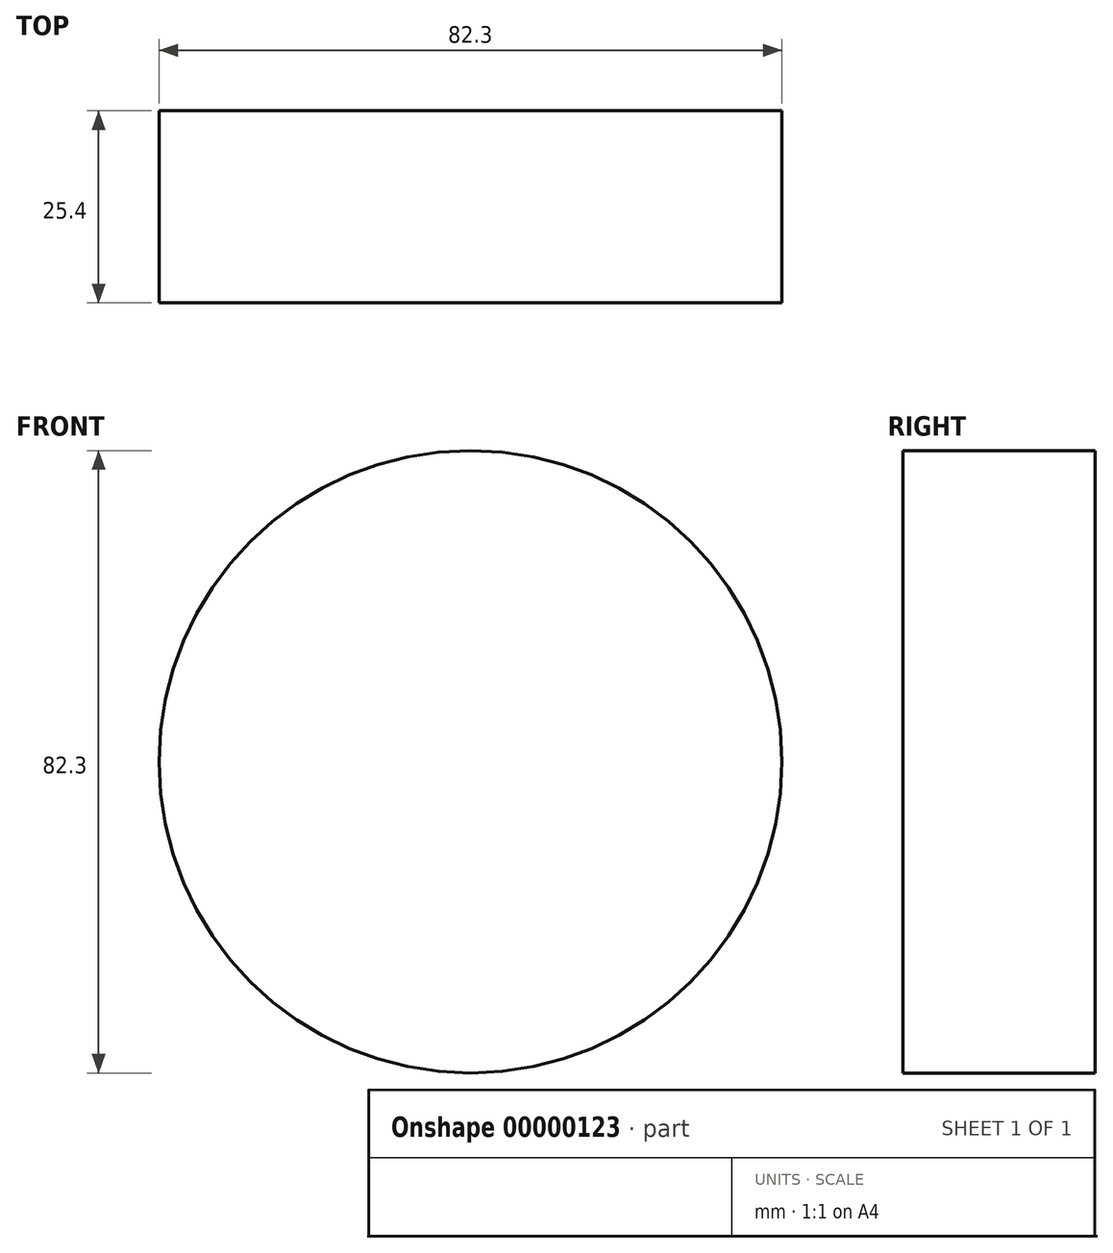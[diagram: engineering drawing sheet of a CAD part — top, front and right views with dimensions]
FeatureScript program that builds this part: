
annotation { "Feature Type Name" : "Feature", "Feature Type Description" : "" }
export const myFeature = defineFeature(function(context is Context, id is Id, definition is map)
    precondition{}
    {
        {
            var Q0;
            Q0=qCreatedBy(makeId("Front.planeOp"),FACE);
            var sketch = newSketch(context, id + "F0", { "sketchPlane" : qUnion([Q0])});
            skCircle(sketch, "E0", {"center": v(0, 0) * mm, "radius": 41.15 * mm});
            skCircle(sketch, "E1", {"center": v(0, 0) * mm, "radius": 21.97 * mm});
            skSolve(sketch);
        }
        {
            var Q0;
            Q0=makeQuery(id+"F0.imprint","IMPRINT",FACE,{"disambiguationData":[TD([[makeQuery(id+"F0.imprint","IMPRINT",EDGE,{"derivedFrom":sQuery(id+"F0.wireOp",EDGE,"E0")}),1.0]])]});
            var Q1;
            Q1=makeQuery(id+"F0.imprint","IMPRINT",FACE,{"disambiguationData":[TD([[makeQuery(id+"F0.imprint","IMPRINT",EDGE,{"derivedFrom":sQuery(id+"F0.wireOp",EDGE,"E1")}),1.0]])]});
            extrude(context, id + "F1", {"entities" : qUnion([Q0, Q1]), "depth" : 25.4 * mm});
        }
    });
